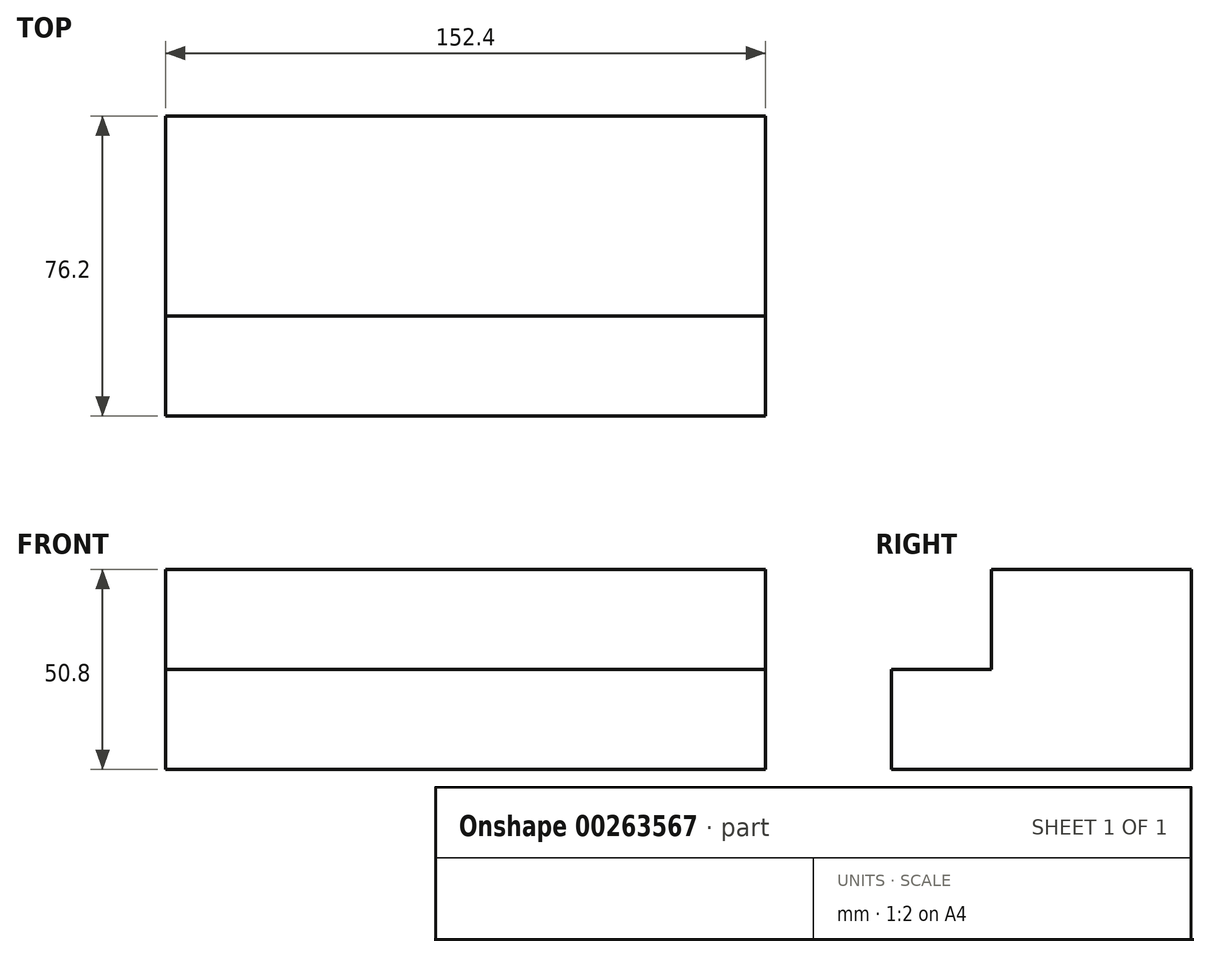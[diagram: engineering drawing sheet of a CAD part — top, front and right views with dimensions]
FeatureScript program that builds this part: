
annotation { "Feature Type Name" : "Feature", "Feature Type Description" : "" }
export const myFeature = defineFeature(function(context is Context, id is Id, definition is map)
    precondition{}
    {
        {
            var Q0;
            Q0=qCreatedBy(makeId("Front.planeOp"),FACE);
            var sketch = newSketch(context, id + "F0", { "sketchPlane" : qUnion([Q0])});
            skLineSegment(sketch, "E0", {"start": v(-57.93, -39.13) * mm, "end": v(94.47, -39.13) * mm});
            skLineSegment(sketch, "E1", {"start": v(-57.93, -39.13) * mm, "end": v(-57.93, -13.73) * mm});
            skLineSegment(sketch, "E2", {"start": v(-57.93, -13.73) * mm, "end": v(94.47, -13.73) * mm});
            skLineSegment(sketch, "E3", {"start": v(94.47, -13.73) * mm, "end": v(94.47, -39.13) * mm});
            skLineSegment(sketch, "E4", {"start": v(-57.93, -13.73) * mm, "end": v(-57.93, 11.67) * mm});
            skLineSegment(sketch, "E5", {"start": v(-57.93, 11.67) * mm, "end": v(94.47, 11.67) * mm});
            skLineSegment(sketch, "E6", {"start": v(94.47, 11.67) * mm, "end": v(94.47, -13.73) * mm});
            skSolve(sketch);
        }
        {
            var Q0;
            Q0 = qSketchRegion(id + "F0", true);
            extrude(context, id + "F1", {"entities" : qUnion([Q0]), "depth" : 76.2 * mm});
        }
        {
            var Q0;
            Q0=makeQuery(id+"F1.opExtrude","SWEPT_FACE",FACE,{"disambiguationData":[OSD([sQuery(id+"F0.wireOp",EDGE,"E3"),sQuery(id+"F0.wireOp",EDGE,"E6")])]});
            var sketch = newSketch(context, id + "F2", { "sketchPlane" : qUnion([Q0])});
            skLineSegment(sketch, "E7.bottom", {"start": v(-76.2, 11.67) * mm, "end": v(-50.8, 11.67) * mm});
            skLineSegment(sketch, "E7.top", {"start": v(-76.2, -13.73) * mm, "end": v(-50.8, -13.73) * mm});
            skLineSegment(sketch, "E7.left", {"start": v(-76.2, 11.67) * mm, "end": v(-76.2, -13.73) * mm});
            skLineSegment(sketch, "E7.right", {"start": v(-50.8, 11.67) * mm, "end": v(-50.8, -13.73) * mm});
            skSolve(sketch);
        }
        {
            var Q0;
            Q0=makeQuery(id+"F2.imprint","IMPRINT",FACE,{"disambiguationData":[TD([[makeQuery(id+"F2.imprint","IMPRINT",EDGE,{"derivedFrom":sQuery(id+"F2.wireOp",EDGE,"E7.bottom")}),-1.0]])]});
            extrude(context, id + "F3", {"entities" : qUnion([Q0]), "operationType" : NewBodyOperationType.REMOVE, "endBound" : BoundingType.UP_TO_NEXT, "oppositeDirection" : true, "depth" : 25.4 * mm});
        }
    });
